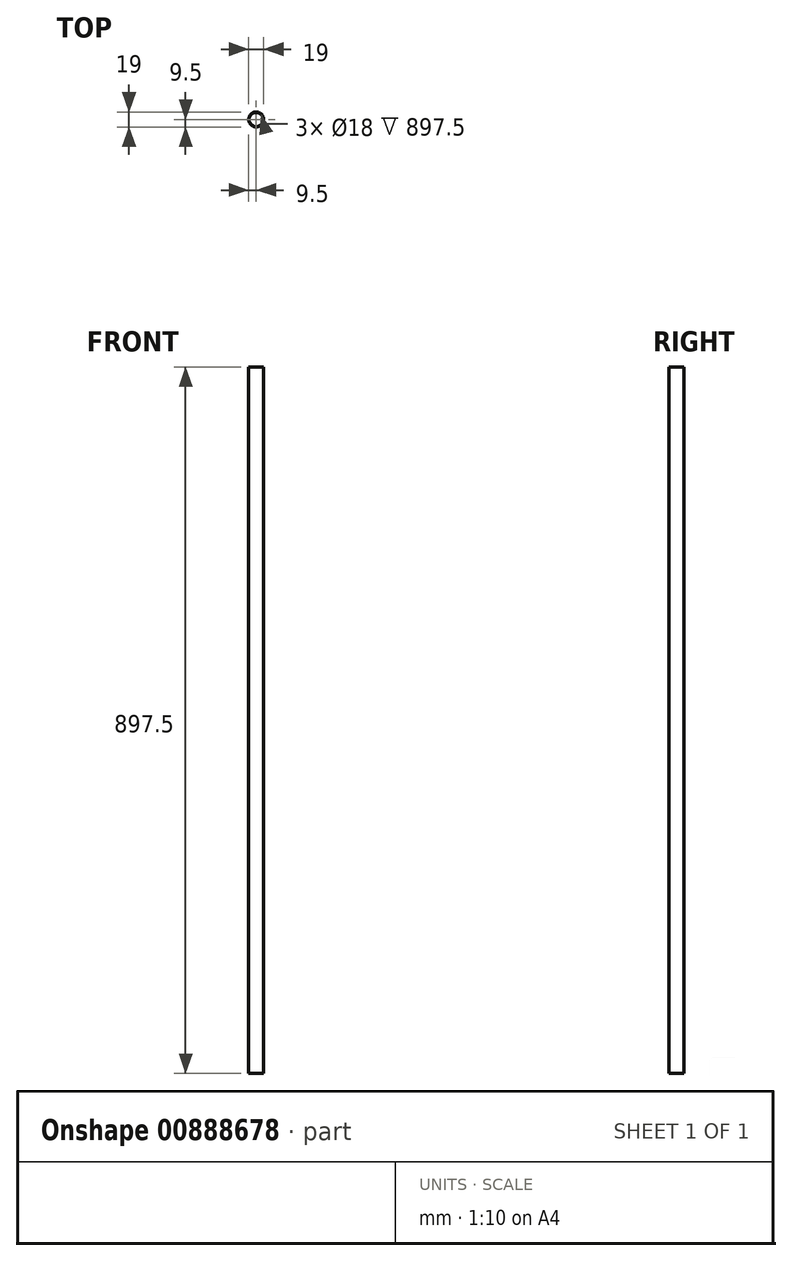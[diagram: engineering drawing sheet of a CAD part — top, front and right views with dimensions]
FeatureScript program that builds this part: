
annotation { "Feature Type Name" : "Feature", "Feature Type Description" : "" }
export const myFeature = defineFeature(function(context is Context, id is Id, definition is map)
    precondition{}
    {
        {
            var Q0;
            Q0=qCreatedBy(makeId("Top.planeOp"),FACE);
            var sketch = newSketch(context, id + "F0", { "sketchPlane" : qUnion([Q0])});
            skCircle(sketch, "E0", {"center": v(0, 0) * mm, "radius": 9.5 * mm});
            skCircle(sketch, "E1", {"center": v(0, 0) * mm, "radius": 9 * mm});
            skSolve(sketch);
        }
        {
            var Q0;
            Q0=makeQuery(id+"F0.imprint","IMPRINT",FACE,{"disambiguationData":[TD([[makeQuery(id+"F0.imprint","IMPRINT",EDGE,{"derivedFrom":sQuery(id+"F0.wireOp",EDGE,"E0")}),1.0]])]});
            extrude(context, id + "F1", {"entities" : qUnion([Q0]), "oppositeDirection" : true, "depth" : 897.5 * mm, "offsetDistance" : 25 * mm});
        }
    });
